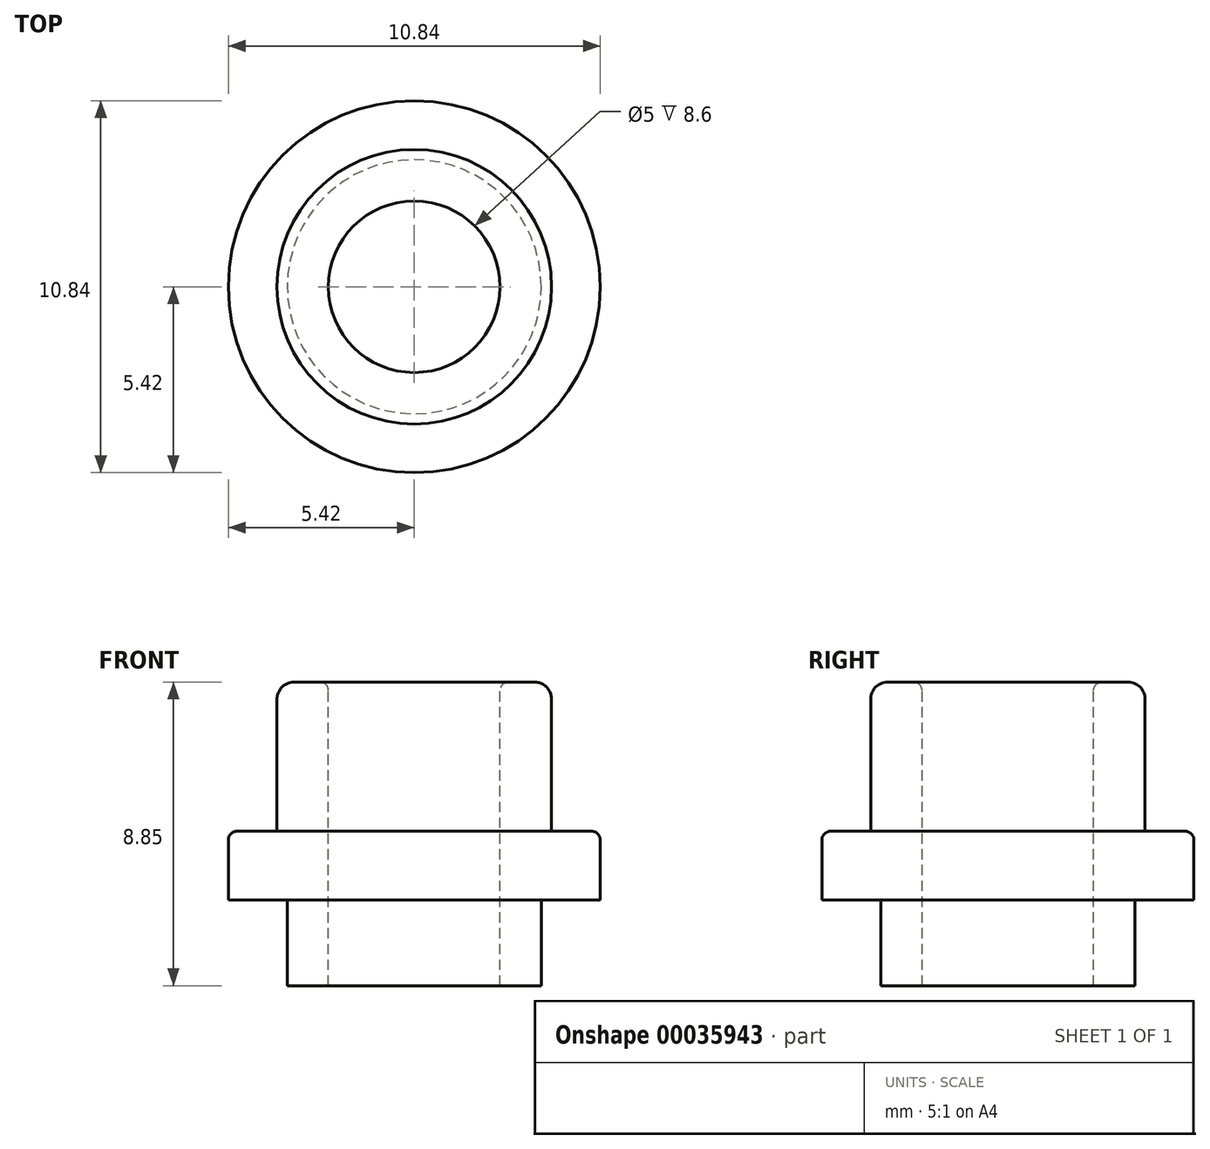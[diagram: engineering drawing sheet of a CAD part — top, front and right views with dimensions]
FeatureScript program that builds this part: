
annotation { "Feature Type Name" : "Feature", "Feature Type Description" : "" }
export const myFeature = defineFeature(function(context is Context, id is Id, definition is map)
    precondition{}
    {
        {
            var Q0;
            Q0=qCreatedBy(makeId("Right.planeOp"),FACE);
            var sketch = newSketch(context, id + "F0", { "sketchPlane" : qUnion([Q0])});
            skLineSegment(sketch, "E0", {"start": v(2.5, 6.35) * mm, "end": v(4, 6.35) * mm});
            skLineSegment(sketch, "E1", {"start": v(4, 6.35) * mm, "end": v(4, 2) * mm});
            skLineSegment(sketch, "E2", {"start": v(4, 2) * mm, "end": v(5.42, 2) * mm});
            skLineSegment(sketch, "E3", {"start": v(5.42, 2) * mm, "end": v(5.42, 0) * mm});
            skLineSegment(sketch, "E4", {"start": v(5.42, 0) * mm, "end": v(3.7, 0) * mm});
            skLineSegment(sketch, "E5", {"start": v(3.7, 0) * mm, "end": v(3.7, -2.5) * mm});
            skLineSegment(sketch, "E6", {"start": v(3.7, -2.5) * mm, "end": v(2.5, -2.5) * mm});
            skLineSegment(sketch, "E7", {"start": v(2.5, -2.5) * mm, "end": v(2.5, 6.35) * mm});
            skLineSegment(sketch, "E8", {"start": v(0, 6.5) * mm, "end": v(0, -9.95) * mm, "construction": true});
            skSolve(sketch);
        }
        {
            var Q0;
            Q0 = qSketchRegion(id + "F0", true);
            var Q1;
            Q1=sQuery(id+"F0.wireOp",EDGE,"E8");
            revolve(context, id + "F1", {"entities" : qUnion([Q0]), "axis" : qUnion([Q1]), "revolveType" : RevolveType.FULL});
        }
        {
            var Q0;
            Q0=makeQuery(id+"F1.opRevolve","SWEPT_EDGE",EDGE,{"disambiguationData":[OSD([sQuery(id+"F0.wireOp",EDGE,"E0"),sQuery(id+"F0.wireOp",EDGE,"E7")])]});
            fillet(context, id + "F2", {"entities" : qUnion([Q0]), "radius" : 0.25 * mm, "tangentPropagation" : true, "allowEdgeOverflow" : false});
        }
        {
            var Q0;
            Q0=makeQuery(id+"F1.opRevolve","SWEPT_EDGE",EDGE,{"disambiguationData":[OSD([sQuery(id+"F0.wireOp",EDGE,"E0"),sQuery(id+"F0.wireOp",EDGE,"E1")])]});
            fillet(context, id + "F3", {"entities" : qUnion([Q0]), "radius" : 0.5 * mm, "tangentPropagation" : true, "allowEdgeOverflow" : false});
        }
        {
            var Q0;
            Q0=makeQuery(id+"F1.opRevolve","SWEPT_EDGE",EDGE,{"disambiguationData":[OSD([sQuery(id+"F0.wireOp",EDGE,"E2"),sQuery(id+"F0.wireOp",EDGE,"E3")])]});
            fillet(context, id + "F4", {"entities" : qUnion([Q0]), "radius" : .25 * mm, "tangentPropagation" : true, "allowEdgeOverflow" : false});
        }
    });
